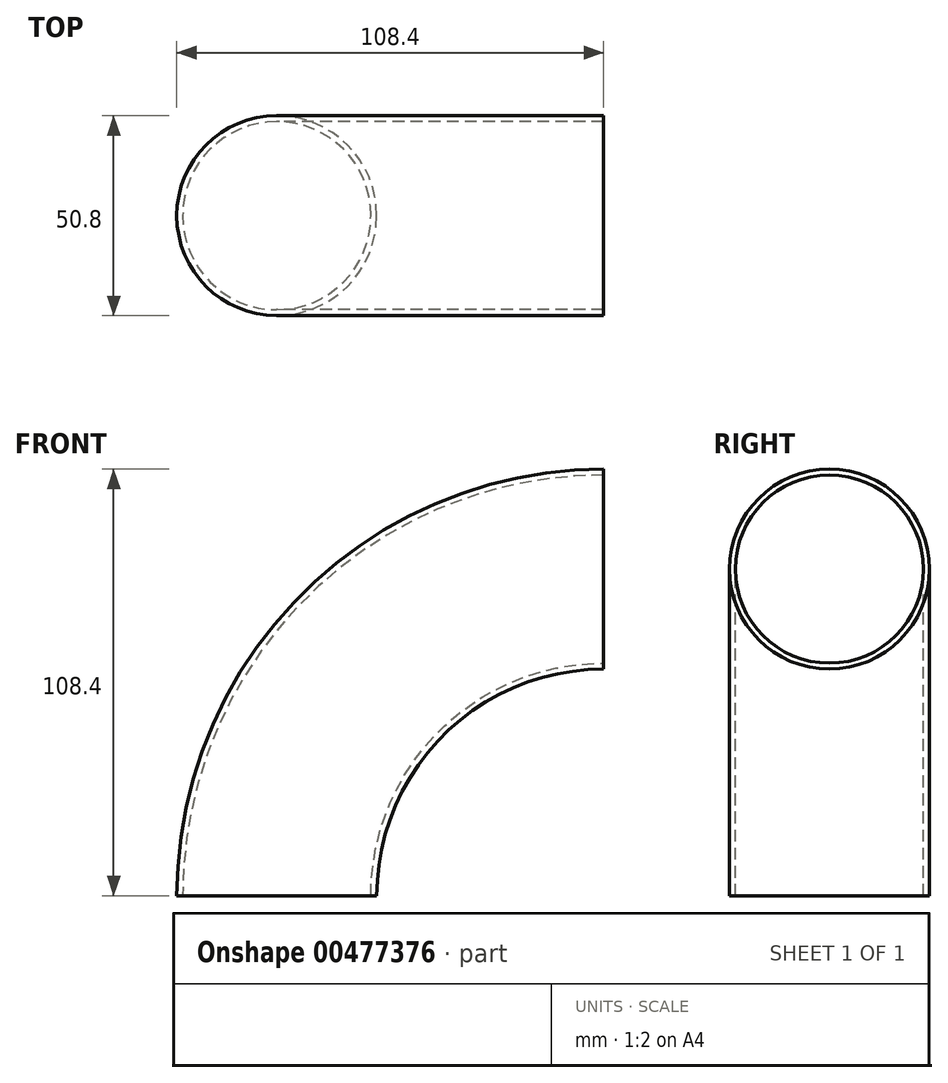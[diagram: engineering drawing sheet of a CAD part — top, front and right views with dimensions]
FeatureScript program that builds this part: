
annotation { "Feature Type Name" : "Feature", "Feature Type Description" : "" }
export const myFeature = defineFeature(function(context is Context, id is Id, definition is map)
    precondition{}
    {
        {
            var Q0;
            Q0=qCreatedBy(makeId("Front.planeOp"),FACE);
            var sketch = newSketch(context, id + "F0", { "sketchPlane" : qUnion([Q0])});
            skArc(sketch, "E0", {"start": v(0, 83) * mm, "mid": v(-58.69, 58.69) * mm, "end": v(-83, 0) * mm});
            skLineSegment(sketch, "E1", {"start": v(0, 0) * mm, "end": v(-83, 0) * mm, "construction": true});
            skLineSegment(sketch, "E2", {"start": v(0, 0) * mm, "end": v(0, 83) * mm, "construction": true});
            skSolve(sketch);
        }
        {
            var Q0;
            Q0=qCreatedBy(makeId("Top.planeOp"),FACE);
            var sketch = newSketch(context, id + "F1", { "sketchPlane" : qUnion([Q0])});
            skCircle(sketch, "E3", {"center": v(-83, 0) * mm, "radius": 23.9 * mm});
            skCircle(sketch, "E4", {"center": v(-83, 0) * mm, "radius": 25.4 * mm});
            skSolve(sketch);
        }
        {
            var Q0;
            Q0=makeQuery(id+"F1.imprint","IMPRINT",FACE,{"disambiguationData":[TD([[makeQuery(id+"F1.imprint","IMPRINT",EDGE,{"derivedFrom":sQuery(id+"F1.wireOp",EDGE,"E3")}),-1.0]])]});
            var Q1;
            Q1=sQuery(id+"F0.wireOp",EDGE,"E0");
            sweep(context, id + "F2", {"profiles" : qUnion([Q0]), "path" : qUnion([Q1])});
        }
    });
